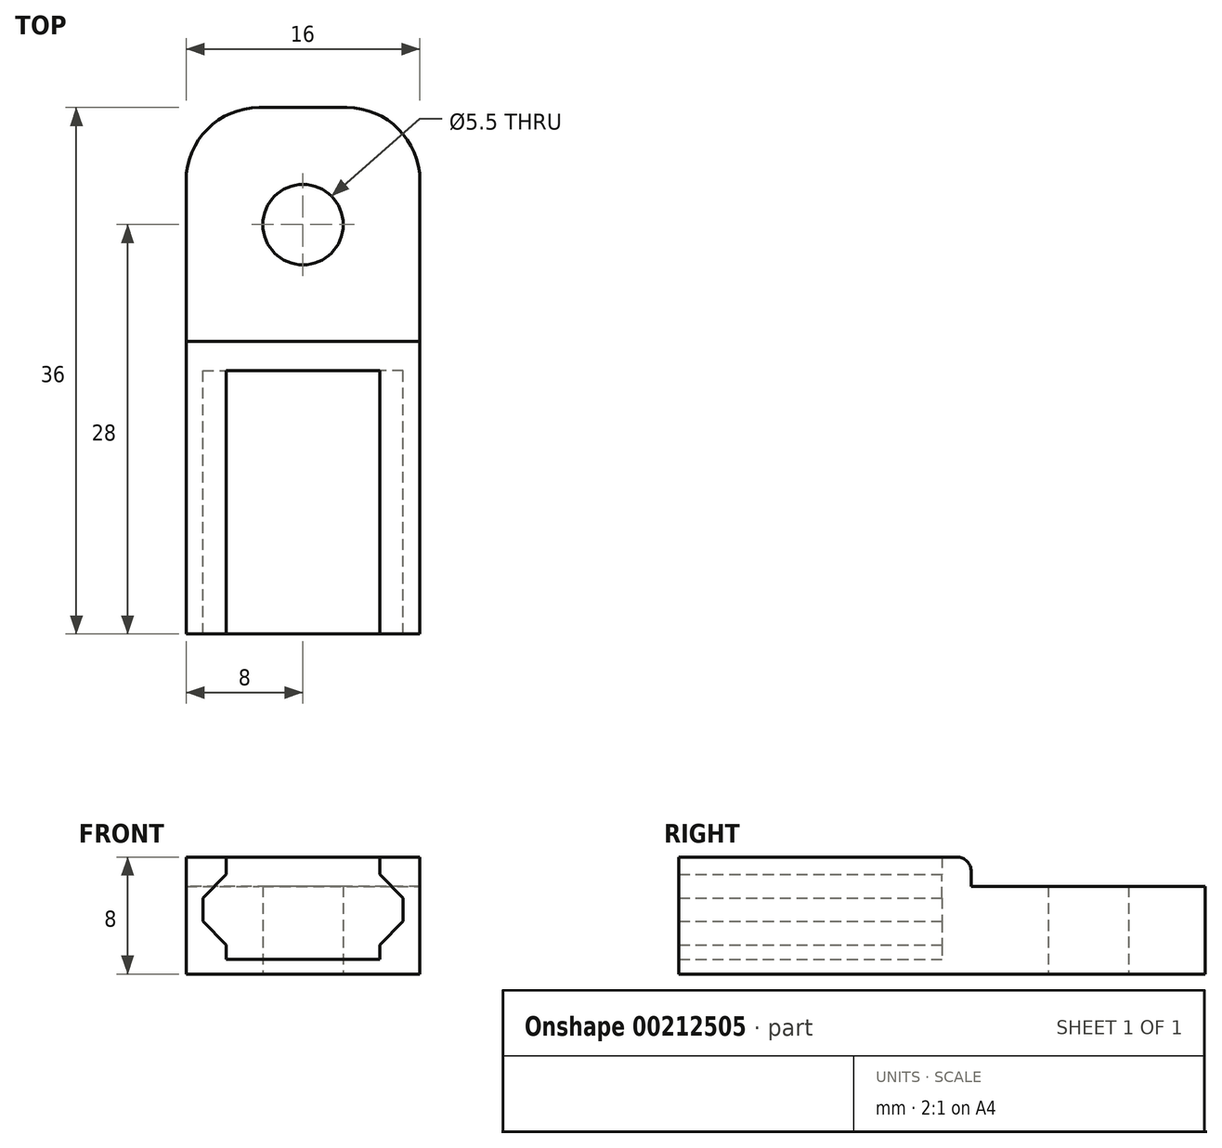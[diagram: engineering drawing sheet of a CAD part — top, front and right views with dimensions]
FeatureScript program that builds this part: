
annotation { "Feature Type Name" : "Feature", "Feature Type Description" : "" }
export const myFeature = defineFeature(function(context is Context, id is Id, definition is map)
    precondition{}
    {
        {
            var Q0;
            Q0=qCreatedBy(makeId("Front.planeOp"),FACE);
            var sketch = newSketch(context, id + "F0", { "sketchPlane" : qUnion([Q0])});
            skPoint(sketch, "E0", {"position": v(-6.85, 0.8) * mm});
            skLineSegment(sketch, "E1", {"start": v(-6.85, 0.8) * mm, "end": v(-5.25, 2.4) * mm});
            skLineSegment(sketch, "E2.MirrorCS", {"start": v(-6.85, -0.8) * mm, "end": v(-5.25, -2.4) * mm});
            skLineSegment(sketch, "E3", {"start": v(-6.85, 0.8) * mm, "end": v(-6.85, -0.8) * mm});
            skPoint(sketch, "E4", {"position": v(-5.25, -3.4) * mm});
            skLineSegment(sketch, "E5", {"start": v(-5.25, -2.4) * mm, "end": v(-5.25, -3.4) * mm});
            skLineSegment(sketch, "E6", {"start": v(-5.25, -3.4) * mm, "end": v(0, -3.4) * mm});
            skLineSegment(sketch, "E7", {"start": v(0, -4.4) * mm, "end": v(-8, -4.4) * mm});
            skLineSegment(sketch, "E8", {"start": v(-8, -4.4) * mm, "end": v(-8, 3.6) * mm});
            skLineSegment(sketch, "E9", {"start": v(-8, 3.6) * mm, "end": v(-5.25, 3.6) * mm});
            skLineSegment(sketch, "E10", {"start": v(-5.25, 3.6) * mm, "end": v(-5.25, 2.4) * mm});
            skLineSegment(sketch, "E11.MirrorCS", {"start": v(5.25, -3.4) * mm, "end": v(0, -3.4) * mm});
            skLineSegment(sketch, "E12.MirrorCS", {"start": v(0, -4.4) * mm, "end": v(8, -4.4) * mm});
            skLineSegment(sketch, "E13.MirrorCS", {"start": v(8, -4.4) * mm, "end": v(8, 3.6) * mm});
            skLineSegment(sketch, "E14.MirrorCS", {"start": v(5.25, -2.4) * mm, "end": v(5.25, -3.4) * mm});
            skLineSegment(sketch, "E15.MirrorCS", {"start": v(6.85, -0.8) * mm, "end": v(5.25, -2.4) * mm});
            skLineSegment(sketch, "E16.MirrorCS", {"start": v(6.85, 0.8) * mm, "end": v(6.85, -0.8) * mm});
            skLineSegment(sketch, "E17.MirrorCS", {"start": v(6.85, 0.8) * mm, "end": v(5.25, 2.4) * mm});
            skLineSegment(sketch, "E18.MirrorCS", {"start": v(5.25, 3.6) * mm, "end": v(5.25, 2.4) * mm});
            skLineSegment(sketch, "E19.MirrorCS", {"start": v(8, 3.6) * mm, "end": v(5.25, 3.6) * mm});
            skSolve(sketch);
        }
        {
            var Q0;
            Q0=makeQuery(id+"F0.imprint","IMPRINT",FACE,{"disambiguationData":[TD([[makeQuery(id+"F0.imprint","IMPRINT",EDGE,{"derivedFrom":sQuery(id+"F0.wireOp",EDGE,"E1")}),1.0]])]});
            extrude(context, id + "F1", {"entities" : qUnion([Q0]), "endBound" : BoundingType.SYMMETRIC, "depth" : 18 * mm});
        }
        {
            var Q0;
            Q0=makeQuery(id+"F1.opExtrude","CAP_FACE",FACE,{"disambiguationData":[OSD([sQuery(id+"F0.wireOp",EDGE,"E1"),sQuery(id+"F0.wireOp",EDGE,"E2.MirrorCS"),sQuery(id+"F0.wireOp",EDGE,"E3"),sQuery(id+"F0.wireOp",EDGE,"E5"),sQuery(id+"F0.wireOp",EDGE,"E6"),sQuery(id+"F0.wireOp",EDGE,"E7"),sQuery(id+"F0.wireOp",EDGE,"E8"),sQuery(id+"F0.wireOp",EDGE,"E9"),sQuery(id+"F0.wireOp",EDGE,"E10"),sQuery(id+"F0.wireOp",EDGE,"E11.MirrorCS"),sQuery(id+"F0.wireOp",EDGE,"E12.MirrorCS"),sQuery(id+"F0.wireOp",EDGE,"E13.MirrorCS"),sQuery(id+"F0.wireOp",EDGE,"E14.MirrorCS"),sQuery(id+"F0.wireOp",EDGE,"E15.MirrorCS"),sQuery(id+"F0.wireOp",EDGE,"E16.MirrorCS"),sQuery(id+"F0.wireOp",EDGE,"E17.MirrorCS"),sQuery(id+"F0.wireOp",EDGE,"E18.MirrorCS"),sQuery(id+"F0.wireOp",EDGE,"E19.MirrorCS")])],"isStart":true});
            var sketch = newSketch(context, id + "F2", { "sketchPlane" : qUnion([Q0])});
            skLineSegment(sketch, "E20", {"start": v(-5.25, 3.6) * mm, "end": v(5.25, 3.6) * mm});
            skSolve(sketch);
        }
        {
            var Q0;
            Q0=makeQuery(id+"F2.imprint","IMPRINT",FACE,{"disambiguationData":[TD([[makeQuery(id+"F2.imprint","IMPRINT",EDGE,{"derivedFrom":makeQuery(id+"F1.opExtrude","CAP_EDGE",EDGE,{"disambiguationData":[OSD([sQuery(id+"F0.wireOp",EDGE,"E1")])],"isStart":true})}),-1.0]])]});
            var Q1;
            Q1=makeQuery(id+"F2.imprint","IMPRINT",FACE,{"disambiguationData":[TD([[makeQuery(id+"F2.imprint","IMPRINT",EDGE,{"derivedFrom":sQuery(id+"F2.wireOp",EDGE,"E20")}),-1.0]])]});
            extrude(context, id + "F3", {"entities" : qUnion([Q0, Q1]), "operationType" : NewBodyOperationType.ADD, "depth" : 2 * mm});
        }
        {
            var Q0;
            {var subQ0=sQuery(id+"F0.wireOp",EDGE,"E12.MirrorCS");var subQ1=sQuery(id+"F0.wireOp",EDGE,"E7");Q0=makeQuery(id+"F3.boolean.opBoolean","MERGE",FACE,{"derivedFrom":[makeQuery(id+"F1.opExtrude","SWEPT_FACE",FACE,{"disambiguationData":[OSD([subQ1,subQ0])]}),makeQuery(id+"F3.opExtrude","SWEPT_FACE",FACE,{"disambiguationData":[OSD([subQ1,subQ0])]})]});}
            var sketch = newSketch(context, id + "F4", { "sketchPlane" : qUnion([Q0])});
            skLineSegment(sketch, "E21.bottom", {"start": v(8, -11) * mm, "end": v(-8, -11) * mm});
            skLineSegment(sketch, "E21.top", {"start": v(8, -27) * mm, "end": v(-8, -27) * mm});
            skLineSegment(sketch, "E21.left", {"start": v(8, -11) * mm, "end": v(8, -27) * mm});
            skLineSegment(sketch, "E21.right", {"start": v(-8, -11) * mm, "end": v(-8, -27) * mm});
            skPoint(sketch, "E21.middle", {"position": v(0, -19) * mm});
            skSolve(sketch);
        }
        {
            var Q0;
            Q0=makeQuery(id+"F4.imprint","IMPRINT",FACE,{"disambiguationData":[TD([[makeQuery(id+"F4.imprint","IMPRINT",EDGE,{"derivedFrom":sQuery(id+"F4.wireOp",EDGE,"E21.bottom")}),1.0]])]});
            extrude(context, id + "F5", {"entities" : qUnion([Q0]), "operationType" : NewBodyOperationType.ADD, "oppositeDirection" : true, "depth" : 6 * mm});
        }
        {
            var Q0;
            Q0=sQuery(id+"F4.wireOp",VERTEX,"E21.middle");
            var Q1;
            Q1=makeQuery(id+"F1.opExtrude","SWEPT_BODY",BODY,{"disambiguationData":[OSD([sQuery(id+"F0.wireOp",EDGE,"E1"),sQuery(id+"F0.wireOp",EDGE,"E2.MirrorCS"),sQuery(id+"F0.wireOp",EDGE,"E3"),sQuery(id+"F0.wireOp",EDGE,"E5"),sQuery(id+"F0.wireOp",EDGE,"E6"),sQuery(id+"F0.wireOp",EDGE,"E7"),sQuery(id+"F0.wireOp",EDGE,"E8"),sQuery(id+"F0.wireOp",EDGE,"E9"),sQuery(id+"F0.wireOp",EDGE,"E10"),sQuery(id+"F0.wireOp",EDGE,"E11.MirrorCS"),sQuery(id+"F0.wireOp",EDGE,"E12.MirrorCS"),sQuery(id+"F0.wireOp",EDGE,"E13.MirrorCS"),sQuery(id+"F0.wireOp",EDGE,"E14.MirrorCS"),sQuery(id+"F0.wireOp",EDGE,"E15.MirrorCS"),sQuery(id+"F0.wireOp",EDGE,"E16.MirrorCS"),sQuery(id+"F0.wireOp",EDGE,"E17.MirrorCS"),sQuery(id+"F0.wireOp",EDGE,"E18.MirrorCS"),sQuery(id+"F0.wireOp",EDGE,"E19.MirrorCS")])]});
            hole(context, id + "F6", {"style" : HoleStyle.SIMPLE, "endStyle" : HoleEndStyle.THROUGH, "standardTappedOrClearance" : lookupTablePath({ "standard" : "ISO", "fit" : "Normal", "size" : "M5", "type" : "Clearance" }), "standardBlindInLast" : lookupTablePath({ "fit" : "Standard", "standard" : "ISO", "size" : "M5", "type" : "Clearance" }), "holeDiameter" : 5.5 * mm, "startFromSketch" : true, "locations" : qUnion([Q0]), "scope" : qUnion([Q1]), "isTappedThrough" : true});
        }
        {
            var Q0;
            Q0=makeQuery(id+"F5.opExtrude","SWEPT_EDGE",EDGE,{"disambiguationData":[OSD([sQuery(id+"F4.wireOp",EDGE,"E21.top"),sQuery(id+"F4.wireOp",EDGE,"E21.left")])]});
            var Q1;
            Q1=makeQuery(id+"F5.opExtrude","SWEPT_EDGE",EDGE,{"disambiguationData":[OSD([sQuery(id+"F4.wireOp",EDGE,"E21.top"),sQuery(id+"F4.wireOp",EDGE,"E21.right")])]});
            fillet(context, id + "F7", {"entities" : qUnion([Q0, Q1]), "radius" : 5 * mm, "tangentPropagation" : true, "allowEdgeOverflow" : false});
        }
        {
            var Q0;
            Q0=makeQuery(id+"F5.opExtrude","CAP_EDGE",EDGE,{"disambiguationData":[OSD([sQuery(id+"F4.wireOp",EDGE,"E21.bottom")])],"isStart":false});
            var Q1;
            Q1=makeQuery(id+"F3.opExtrude","CAP_EDGE",EDGE,{"disambiguationData":[OSD([sQuery(id+"F0.wireOp",EDGE,"E9"),sQuery(id+"F0.wireOp",EDGE,"E19.MirrorCS"),sQuery(id+"F2.wireOp",EDGE,"E20")])],"isStart":false});
            fillet(context, id + "F8", {"entities" : qUnion([Q0, Q1]), "radius" : 1 * mm, "tangentPropagation" : true, "allowEdgeOverflow" : false});
        }
    });
